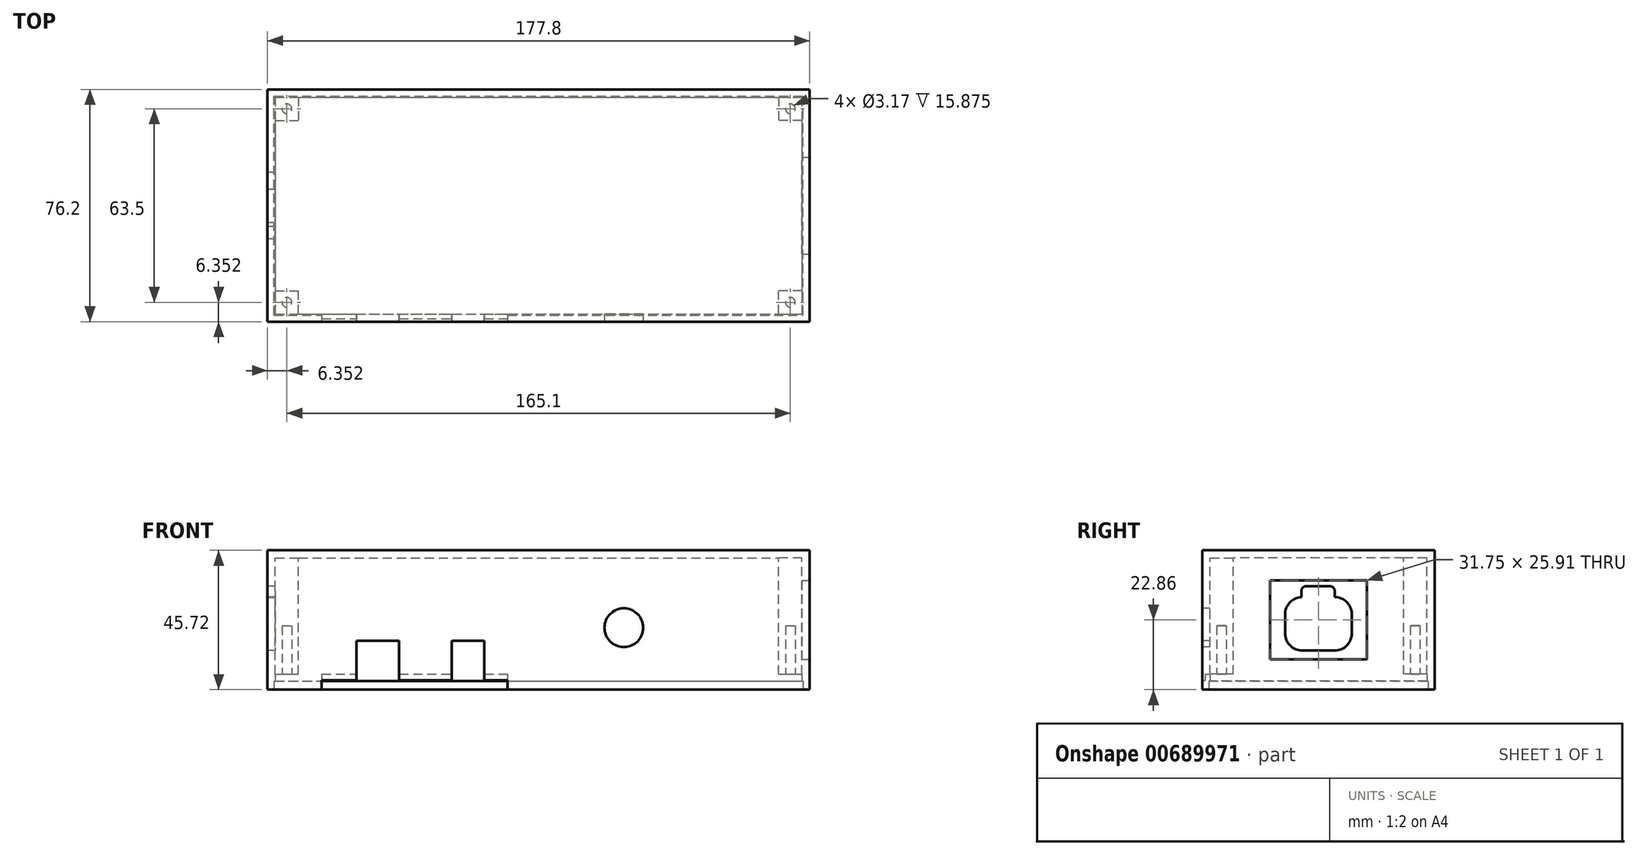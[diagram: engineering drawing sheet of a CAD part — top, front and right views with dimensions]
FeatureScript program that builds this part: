
annotation { "Feature Type Name" : "Feature", "Feature Type Description" : "" }
export const myFeature = defineFeature(function(context is Context, id is Id, definition is map)
    precondition{}
    {
        {
            var Q0;
            Q0=qCreatedBy(makeId("Top.planeOp"),FACE);
            var sketch = newSketch(context, id + "F0", { "sketchPlane" : qUnion([Q0])});
            skLineSegment(sketch, "E0.bottom", {"start": v(-143.67, 49.46) * mm, "end": v(34.13, 49.46) * mm});
            skLineSegment(sketch, "E0.top", {"start": v(-143.67, -26.74) * mm, "end": v(34.13, -26.74) * mm});
            skLineSegment(sketch, "E0.left", {"start": v(-143.67, 49.46) * mm, "end": v(-143.67, -26.74) * mm});
            skLineSegment(sketch, "E0.right", {"start": v(34.13, 49.46) * mm, "end": v(34.13, -26.74) * mm});
            skSolve(sketch);
        }
        {
            var Q0;
            Q0=makeQuery(id+"F0.imprint","IMPRINT",FACE,{"disambiguationData":[TD([[makeQuery(id+"F0.imprint","IMPRINT",EDGE,{"derivedFrom":sQuery(id+"F0.wireOp",EDGE,"E0.bottom")}),-1.0]])]});
            extrude(context, id + "F1", {"entities" : qUnion([Q0]), "depth" : 45.72 * mm, "offsetDistance" : 25.4 * mm});
        }
        {
            var Q0;
            Q0=makeQuery(id+"F1.opExtrude","CAP_FACE",FACE,{"disambiguationData":[OSD([sQuery(id+"F0.wireOp",EDGE,"E0.bottom"),sQuery(id+"F0.wireOp",EDGE,"E0.top"),sQuery(id+"F0.wireOp",EDGE,"E0.left"),sQuery(id+"F0.wireOp",EDGE,"E0.right")])],"isStart":true});
            shell(context, id + "F2", {"entities" : qUnion([Q0]), "thickness" : 2.54 * mm});
        }
        {
            var Q0;
            Q0=makeQuery(id+"F1.opExtrude","SWEPT_FACE",FACE,{"disambiguationData":[OSD([sQuery(id+"F0.wireOp",EDGE,"E0.top")])]});
            var sketch = newSketch(context, id + "F3", { "sketchPlane" : qUnion([Q0])});
            skLineSegment(sketch, "E1.bottom", {"start": v(-114.46, 0) * mm, "end": v(-100.49, 0) * mm});
            skLineSegment(sketch, "E1.top", {"start": v(-114.46, 16) * mm, "end": v(-100.49, 16) * mm});
            skLineSegment(sketch, "E1.left", {"start": v(-114.46, 0) * mm, "end": v(-114.46, 16) * mm});
            skLineSegment(sketch, "E1.right", {"start": v(-100.49, 0) * mm, "end": v(-100.49, 16) * mm});
            skLineSegment(sketch, "E2.bottom", {"start": v(-83.22, 0) * mm, "end": v(-72.55, 0) * mm});
            skLineSegment(sketch, "E2.top", {"start": v(-83.22, 16) * mm, "end": v(-72.55, 16) * mm});
            skLineSegment(sketch, "E2.left", {"start": v(-83.22, 0) * mm, "end": v(-83.22, 16) * mm});
            skLineSegment(sketch, "E2.right", {"start": v(-72.55, 0) * mm, "end": v(-72.55, 16) * mm});
            skSolve(sketch);
        }
        {
            var Q0;
            Q0=makeQuery(id+"F3.imprint","IMPRINT",FACE,{"disambiguationData":[TD([[makeQuery(id+"F3.imprint","IMPRINT",EDGE,{"derivedFrom":sQuery(id+"F3.wireOp",EDGE,"E1.bottom")}),1.0]])]});
            var Q1;
            Q1=makeQuery(id+"F3.imprint","IMPRINT",FACE,{"disambiguationData":[TD([[makeQuery(id+"F3.imprint","IMPRINT",EDGE,{"derivedFrom":sQuery(id+"F3.wireOp",EDGE,"E2.bottom")}),1.0]])]});
            extrude(context, id + "F4", {"entities" : qUnion([Q0, Q1]), "operationType" : NewBodyOperationType.REMOVE, "oppositeDirection" : true, "depth" : 2.54 * mm, "offsetDistance" : 25.4 * mm});
        }
        {
            var Q0;
            {var subQ0=sQuery(id+"F0.wireOp",EDGE,"E0.left");var subQ1=sQuery(id+"F0.wireOp",EDGE,"E0.bottom");var subQ2=sQuery(id+"F0.wireOp",EDGE,"E0.top");var subQ3=sQuery(id+"F0.wireOp",EDGE,"E0.right");Q0=makeQuery(id+"F4.boolean.opBoolean","SPLIT",FACE,{"disambiguationData":[TD([makeQuery(id+"F1.opExtrude","SWEPT_FACE",FACE,{"disambiguationData":[OSD([subQ1])]})])],"derivedFrom":makeQuery(id+"F1.opExtrude","CAP_FACE",FACE,{"disambiguationData":[OSD([subQ1,subQ2,subQ0,subQ3])],"isStart":true})});}
            var sketch = newSketch(context, id + "F5", { "sketchPlane" : qUnion([Q0])});
            skLineSegment(sketch, "E3.bottom", {"start": v(-125.89, 24.2) * mm, "end": v(-64.93, 24.2) * mm});
            skLineSegment(sketch, "E3.top", {"start": v(-125.89, 26.74) * mm, "end": v(-64.93, 26.74) * mm});
            skLineSegment(sketch, "E3.left", {"start": v(-125.89, 24.2) * mm, "end": v(-125.89, 26.74) * mm});
            skLineSegment(sketch, "E3.right", {"start": v(-64.93, 24.2) * mm, "end": v(-64.93, 26.74) * mm});
            skSolve(sketch);
        }
        {
            var Q0;
            {var subQ5=sQuery(id+"F5.wireOp",EDGE,"E3.left");Q0=makeQuery(id+"F5.imprint","IMPRINT",FACE,{"disambiguationData":[TD([[makeQuery(id+"F5.imprint","IMPRINT",EDGE,{"derivedFrom":subQ5}),-1.0]])]});}
            var Q1;
            {var subQ0=sQuery(id+"F5.wireOp",EDGE,"E3.bottom");var subQ1=sQuery(id+"F0.wireOp",EDGE,"E0.top");var subQ2=makeQuery(id+"F4.boolean.opBoolean","COPY",EDGE,{"derivedFrom":makeQuery(id+"F4.opExtrude","SWEPT_EDGE",EDGE,{"disambiguationData":[OSD([subQ1,sQuery(id+"F3.wireOp",EDGE,"E1.bottom"),sQuery(id+"F3.wireOp",EDGE,"E1.left")])]})});var subQ3=makeQuery(id+"F5.imprint","INTERSECT",VERTEX,{"derivedFrom":[subQ2,subQ0]});Q1=makeQuery(id+"F5.imprint","IMPRINT",FACE,{"disambiguationData":[TD([[makeQuery(id+"F5.imprint","IMPRINT",EDGE,{"disambiguationData":[TD([[subQ3,-1.0]])],"derivedFrom":subQ0}),1.0]])]});}
            var Q2;
            {var subQ5=sQuery(id+"F5.wireOp",EDGE,"E3.right");Q2=makeQuery(id+"F5.imprint","IMPRINT",FACE,{"disambiguationData":[TD([[makeQuery(id+"F5.imprint","IMPRINT",EDGE,{"derivedFrom":subQ5}),1.0]])]});}
            extrude(context, id + "F6", {"entities" : qUnion([Q0, Q1, Q2]), "operationType" : NewBodyOperationType.REMOVE, "oppositeDirection" : true, "depth" : 3.05 * mm, "offsetDistance" : 25.4 * mm});
        }
        {
            var Q0;
            Q0=makeQuery(id+"F1.opExtrude","SWEPT_FACE",FACE,{"disambiguationData":[OSD([sQuery(id+"F0.wireOp",EDGE,"E0.left")])]});
            var sketch = newSketch(context, id + "F7", { "sketchPlane" : qUnion([Q0])});
            skLineSegment(sketch, "E4.bottom", {"start": v(-16.7, 30.35) * mm, "end": v(-6.04, 30.35) * mm});
            skLineSegment(sketch, "E4.top", {"start": v(-16.7, 12.83) * mm, "end": v(-6.03, 12.83) * mm});
            skLineSegment(sketch, "E4.left", {"start": v(-22.28, 24.77) * mm, "end": v(-22.28, 18.41) * mm});
            skLineSegment(sketch, "E4.right", {"start": v(-0.44, 24.77) * mm, "end": v(-0.44, 18.41) * mm});
            skPoint(sketch, "E5.visualSharp", {"position": v(-22.28, 30.35) * mm});
            skArc(sketch, "E5.filletArc", {"start": v(-16.7, 30.35) * mm, "mid": v(-20.65, 28.72) * mm, "end": v(-22.28, 24.77) * mm});
            skPoint(sketch, "E6.visualSharp", {"position": v(-0.44, 30.35) * mm});
            skArc(sketch, "E6.filletArc", {"start": v(-0.44, 24.77) * mm, "mid": v(-1.56, 28.12) * mm, "end": v(-4.46, 30.13) * mm});
            skPoint(sketch, "E7.visualSharp", {"position": v(-0.44, 12.83) * mm});
            skArc(sketch, "E7.filletArc", {"start": v(-6.03, 12.83) * mm, "mid": v(-2.08, 14.46) * mm, "end": v(-0.44, 18.41) * mm});
            skPoint(sketch, "E8.visualSharp", {"position": v(-22.28, 12.83) * mm});
            skArc(sketch, "E8.filletArc", {"start": v(-22.28, 18.41) * mm, "mid": v(-20.65, 14.46) * mm, "end": v(-16.7, 12.83) * mm});
            skLineSegment(sketch, "E9.bottom", {"start": v(-15.17, 33.9) * mm, "end": v(-7.3, 33.9) * mm});
            skLineSegment(sketch, "E9.top", {"start": v(-16.7, 30.35) * mm, "end": v(-5.77, 30.35) * mm});
            skLineSegment(sketch, "E9.left", {"start": v(-16.7, 32.39) * mm, "end": v(-16.7, 30.35) * mm});
            skLineSegment(sketch, "E9.right", {"start": v(-5.77, 32.39) * mm, "end": v(-5.77, 30.35) * mm});
            skPoint(sketch, "E10.visualSharp", {"position": v(-16.7, 33.9) * mm});
            skArc(sketch, "E10.filletArc", {"start": v(-15.17, 33.9) * mm, "mid": v(-16.25, 33.46) * mm, "end": v(-16.7, 32.39) * mm});
            skPoint(sketch, "E11.visualSharp", {"position": v(-5.77, 33.9) * mm});
            skArc(sketch, "E11.filletArc", {"start": v(-5.77, 32.39) * mm, "mid": v(-6.22, 33.46) * mm, "end": v(-7.3, 33.9) * mm});
            skLineSegment(sketch, "E12", {"start": v(-5.77, 30.35) * mm, "end": v(-4.46, 30.13) * mm});
            skLineSegment(sketch, "E13", {"start": v(26.74, 22.86) * mm, "end": v(-0.44, 22.86) * mm, "construction": true});
            skPoint(sketch, "E13.endSnap0", {"position": v(-0.44, 21.59) * mm});
            skLineSegment(sketch, "E14", {"start": v(-11.36, 0) * mm, "end": v(-11.36, 12.83) * mm, "construction": true});
            skLineSegment(sketch, "E15", {"start": v(-16.7, 24.77) * mm, "end": v(-6.03, 18.41) * mm, "construction": true});
            skLineSegment(sketch, "E16", {"start": v(-6.03, 24.77) * mm, "end": v(-16.7, 18.41) * mm, "construction": true});
            skLineSegment(sketch, "E17.bottom", {"start": v(-0.44, 30.35) * mm, "end": v(-22.28, 30.35) * mm});
            skLineSegment(sketch, "E17.top", {"start": v(-0.44, 12.83) * mm, "end": v(-22.28, 12.83) * mm});
            skLineSegment(sketch, "E17.left", {"start": v(-0.44, 30.35) * mm, "end": v(-0.44, 12.83) * mm});
            skLineSegment(sketch, "E17.right", {"start": v(-22.28, 30.35) * mm, "end": v(-22.28, 12.83) * mm});
            skPoint(sketch, "E18", {"position": v(-11.36, 21.6) * mm});
            skSolve(sketch);
        }
        {
            var Q0;
            Q0=makeQuery(id+"F7.imprint","IMPRINT",FACE,{"disambiguationData":[TD([[makeQuery(id+"F7.imprint","IMPRINT",EDGE,{"derivedFrom":sQuery(id+"F7.wireOp",EDGE,"E9.bottom")}),-1.0]])]});
            var Q1;
            {var subQ4=sQuery(id+"F7.wireOp",EDGE,"E5.filletArc");Q1=makeQuery(id+"F7.imprint","IMPRINT",FACE,{"disambiguationData":[TD([[makeQuery(id+"F7.imprint","IMPRINT",EDGE,{"derivedFrom":subQ4}),1.0]])]});}
            extrude(context, id + "F8", {"entities" : qUnion([Q0, Q1]), "operationType" : NewBodyOperationType.REMOVE, "oppositeDirection" : true, "depth" : 2.54 * mm, "offsetDistance" : 25.4 * mm});
        }
        {
            var Q0;
            Q0=makeQuery(id+"F1.opExtrude","SWEPT_FACE",FACE,{"disambiguationData":[OSD([sQuery(id+"F0.wireOp",EDGE,"E0.right")])]});
            var sketch = newSketch(context, id + "F9", { "sketchPlane" : qUnion([Q0])});
            skLineSegment(sketch, "E19.bottom", {"start": v(-4.51, 35.81) * mm, "end": v(27.24, 35.81) * mm});
            skLineSegment(sketch, "E19.top", {"start": v(-4.51, 9.9) * mm, "end": v(27.24, 9.9) * mm});
            skLineSegment(sketch, "E19.left", {"start": v(-4.51, 35.81) * mm, "end": v(-4.51, 9.9) * mm});
            skLineSegment(sketch, "E19.right", {"start": v(27.24, 35.81) * mm, "end": v(27.24, 9.9) * mm});
            skLineSegment(sketch, "E20", {"start": v(27.24, 22.86) * mm, "end": v(49.46, 22.86) * mm, "construction": true});
            skLineSegment(sketch, "E21", {"start": v(11.36, 9.9) * mm, "end": v(11.36, 0) * mm, "construction": true});
            skSolve(sketch);
        }
        {
            var Q0;
            Q0=makeQuery(id+"F9.imprint","IMPRINT",FACE,{"disambiguationData":[TD([[makeQuery(id+"F9.imprint","IMPRINT",EDGE,{"derivedFrom":sQuery(id+"F9.wireOp",EDGE,"E19.bottom")}),-1.0]])]});
            extrude(context, id + "F10", {"entities" : qUnion([Q0]), "operationType" : NewBodyOperationType.REMOVE, "oppositeDirection" : true, "depth" : 2.54 * mm, "offsetDistance" : 25.4 * mm});
        }
        {
            var Q0;
            {var subQ0=sQuery(id+"F0.wireOp",EDGE,"E0.left");var subQ1=sQuery(id+"F0.wireOp",EDGE,"E0.bottom");var subQ2=sQuery(id+"F0.wireOp",EDGE,"E0.top");var subQ3=sQuery(id+"F0.wireOp",EDGE,"E0.right");Q0=makeQuery(id+"F4.boolean.opBoolean","SPLIT",FACE,{"disambiguationData":[TD([makeQuery(id+"F1.opExtrude","SWEPT_FACE",FACE,{"disambiguationData":[OSD([subQ1])]})])],"derivedFrom":makeQuery(id+"F1.opExtrude","CAP_FACE",FACE,{"disambiguationData":[OSD([subQ1,subQ2,subQ0,subQ3])],"isStart":true})});}
            var sketch = newSketch(context, id + "F11", { "sketchPlane" : qUnion([Q0])});
            skPoint(sketch, "E22.firstSnap0", {"position": v(-125.89, 25.75) * mm});
            skLineSegment(sketch, "E22.bottom", {"start": v(-125.89, 25.75) * mm, "end": v(-62.39, 25.75) * mm});
            skLineSegment(sketch, "E22.top", {"start": v(-125.89, 24.2) * mm, "end": v(-62.39, 24.2) * mm});
            skLineSegment(sketch, "E22.left", {"start": v(-125.89, 25.75) * mm, "end": v(-125.89, 24.2) * mm});
            skLineSegment(sketch, "E22.right", {"start": v(-62.39, 25.75) * mm, "end": v(-62.39, 24.2) * mm});
            skSolve(sketch);
        }
        {
            var Q0;
            {var subQ0=sQuery(id+"F11.wireOp",EDGE,"E22.left");Q0=makeQuery(id+"F11.imprint","IMPRINT",FACE,{"disambiguationData":[TD([[makeQuery(id+"F11.imprint","IMPRINT",EDGE,{"derivedFrom":subQ0}),-1.0]])]});}
            extrude(context, id + "F12", {"entities" : qUnion([Q0]), "operationType" : NewBodyOperationType.REMOVE, "oppositeDirection" : true, "depth" : 5.08 * mm, "offsetDistance" : 25.4 * mm});
        }
        {
            var Q0;
            Q0=makeQuery(id+"F2.opShell","OFFSET_FACE",FACE,{"disambiguationData":[OSD([sQuery(id+"F0.wireOp",EDGE,"E0.bottom"),sQuery(id+"F0.wireOp",EDGE,"E0.top"),sQuery(id+"F0.wireOp",EDGE,"E0.left"),sQuery(id+"F0.wireOp",EDGE,"E0.right")])]});
            var sketch = newSketch(context, id + "F13", { "sketchPlane" : qUnion([Q0])});
            skLineSegment(sketch, "E23.bottom", {"start": v(-141.13, 24.2) * mm, "end": v(-133.5, 24.2) * mm});
            skLineSegment(sketch, "E23.top", {"start": v(-141.13, 16.58) * mm, "end": v(-133.5, 16.58) * mm});
            skLineSegment(sketch, "E23.left", {"start": v(-141.13, 24.2) * mm, "end": v(-141.13, 16.58) * mm});
            skLineSegment(sketch, "E23.right", {"start": v(-133.5, 24.2) * mm, "end": v(-133.5, 16.58) * mm});
            skLineSegment(sketch, "E24.bottom", {"start": v(31.6, 24.2) * mm, "end": v(23.97, 24.2) * mm});
            skLineSegment(sketch, "E24.top", {"start": v(31.6, 16.58) * mm, "end": v(23.97, 16.58) * mm});
            skLineSegment(sketch, "E24.left", {"start": v(31.6, 24.2) * mm, "end": v(31.6, 16.58) * mm});
            skLineSegment(sketch, "E24.right", {"start": v(23.97, 24.2) * mm, "end": v(23.97, 16.58) * mm});
            skLineSegment(sketch, "E25.bottom", {"start": v(31.6, -46.92) * mm, "end": v(23.97, -46.92) * mm});
            skLineSegment(sketch, "E25.top", {"start": v(31.6, -39.3) * mm, "end": v(23.97, -39.3) * mm});
            skLineSegment(sketch, "E25.left", {"start": v(31.6, -46.92) * mm, "end": v(31.6, -39.3) * mm});
            skLineSegment(sketch, "E25.right", {"start": v(23.97, -46.92) * mm, "end": v(23.97, -39.3) * mm});
            skLineSegment(sketch, "E26.bottom", {"start": v(-141.13, -46.92) * mm, "end": v(-133.5, -46.92) * mm});
            skLineSegment(sketch, "E26.top", {"start": v(-141.13, -39.3) * mm, "end": v(-133.5, -39.3) * mm});
            skLineSegment(sketch, "E26.left", {"start": v(-141.13, -46.92) * mm, "end": v(-141.13, -39.3) * mm});
            skLineSegment(sketch, "E26.right", {"start": v(-133.5, -46.92) * mm, "end": v(-133.5, -39.3) * mm});
            skSolve(sketch);
        }
        {
            var Q0;
            Q0=makeQuery(id+"F13.imprint","IMPRINT",FACE,{"disambiguationData":[TD([[makeQuery(id+"F13.imprint","IMPRINT",EDGE,{"derivedFrom":sQuery(id+"F13.wireOp",EDGE,"E24.bottom")}),-1.0]])]});
            var Q1;
            Q1=makeQuery(id+"F13.imprint","IMPRINT",FACE,{"disambiguationData":[TD([[makeQuery(id+"F13.imprint","IMPRINT",EDGE,{"derivedFrom":sQuery(id+"F13.wireOp",EDGE,"E25.bottom")}),1.0]])]});
            var Q2;
            Q2=makeQuery(id+"F13.imprint","IMPRINT",FACE,{"disambiguationData":[TD([[makeQuery(id+"F13.imprint","IMPRINT",EDGE,{"derivedFrom":sQuery(id+"F13.wireOp",EDGE,"E23.bottom")}),-1.0]])]});
            var Q3;
            Q3=makeQuery(id+"F13.imprint","IMPRINT",FACE,{"disambiguationData":[TD([[makeQuery(id+"F13.imprint","IMPRINT",EDGE,{"derivedFrom":sQuery(id+"F13.wireOp",EDGE,"E26.bottom")}),1.0]])]});
            extrude(context, id + "F14", {"entities" : qUnion([Q0, Q1, Q2, Q3]), "operationType" : NewBodyOperationType.ADD, "depth" : 38.1 * mm, "offsetDistance" : 25.4 * mm});
        }
        {
            var Q0;
            Q0=makeQuery(id+"F14.opExtrude","CAP_FACE",FACE,{"disambiguationData":[OSD([sQuery(id+"F13.wireOp",EDGE,"E23.bottom"),sQuery(id+"F13.wireOp",EDGE,"E23.top"),sQuery(id+"F13.wireOp",EDGE,"E23.left"),sQuery(id+"F13.wireOp",EDGE,"E23.right")])],"isStart":false});
            var sketch = newSketch(context, id + "F15", { "sketchPlane" : qUnion([Q0])});
            skCircle(sketch, "E27", {"center": v(-137.32, 20.39) * mm, "radius": 1.59 * mm});
            skPoint(sketch, "E27.centerSnap0", {"position": v(-137.32, 24.2) * mm});
            skPoint(sketch, "E27.centerSnap1", {"position": v(-133.5, 20.39) * mm});
            skCircle(sketch, "E28", {"center": v(27.78, 20.39) * mm, "radius": 1.59 * mm});
            skCircle(sketch, "E29", {"center": v(-137.32, -43.11) * mm, "radius": 1.59 * mm});
            skCircle(sketch, "E30", {"center": v(27.78, -43.11) * mm, "radius": 1.59 * mm});
            skSolve(sketch);
        }
        {
            var Q0;
            Q0=makeQuery(id+"F15.imprint","IMPRINT",FACE,{"disambiguationData":[TD([[makeQuery(id+"F15.imprint","IMPRINT",EDGE,{"derivedFrom":sQuery(id+"F15.wireOp",EDGE,"E27")}),1.0]])]});
            var Q1;
            Q1=makeQuery(id+"F15.imprint","IMPRINT",FACE,{"disambiguationData":[TD([[makeQuery(id+"F15.imprint","IMPRINT",EDGE,{"derivedFrom":sQuery(id+"F15.wireOp",EDGE,"E29")}),1.0]])]});
            var Q2;
            Q2=makeQuery(id+"F15.imprint","IMPRINT",FACE,{"disambiguationData":[TD([[makeQuery(id+"F15.imprint","IMPRINT",EDGE,{"derivedFrom":sQuery(id+"F15.wireOp",EDGE,"E28")}),1.0]])]});
            var Q3;
            Q3=makeQuery(id+"F15.imprint","IMPRINT",FACE,{"disambiguationData":[TD([[makeQuery(id+"F15.imprint","IMPRINT",EDGE,{"derivedFrom":sQuery(id+"F15.wireOp",EDGE,"E30")}),1.0]])]});
            extrude(context, id + "F16", {"entities" : qUnion([Q0, Q1, Q2, Q3]), "operationType" : NewBodyOperationType.REMOVE, "oppositeDirection" : true, "depth" : 15.88 * mm, "offsetDistance" : 25.4 * mm});
        }
        {
            var Q0;
            Q0=makeQuery(id+"F1.opExtrude","SWEPT_FACE",FACE,{"disambiguationData":[OSD([sQuery(id+"F0.wireOp",EDGE,"E0.top")])]});
            var sketch = newSketch(context, id + "F17", { "sketchPlane" : qUnion([Q0])});
            skCircle(sketch, "E31", {"center": v(-26.83, 20.32) * mm, "radius": 6.35 * mm});
            skSolve(sketch);
        }
        {
            var Q0;
            Q0=makeQuery(id+"F17.imprint","IMPRINT",FACE,{"disambiguationData":[TD([[makeQuery(id+"F17.imprint","IMPRINT",EDGE,{"derivedFrom":sQuery(id+"F17.wireOp",EDGE,"E31")}),1.0]])]});
            extrude(context, id + "F18", {"entities" : qUnion([Q0]), "operationType" : NewBodyOperationType.REMOVE, "oppositeDirection" : true, "depth" : 2.54 * mm, "offsetDistance" : 25.4 * mm});
        }
        {
            var Q0;
            {var subQ0=sQuery(id+"F0.wireOp",EDGE,"E0.left");var subQ1=sQuery(id+"F0.wireOp",EDGE,"E0.bottom");var subQ2=sQuery(id+"F0.wireOp",EDGE,"E0.top");var subQ3=sQuery(id+"F0.wireOp",EDGE,"E0.right");Q0=makeQuery(id+"F4.boolean.opBoolean","SPLIT",FACE,{"disambiguationData":[TD([makeQuery(id+"F1.opExtrude","SWEPT_FACE",FACE,{"disambiguationData":[OSD([subQ1])]})])],"derivedFrom":makeQuery(id+"F1.opExtrude","CAP_FACE",FACE,{"disambiguationData":[OSD([subQ1,subQ2,subQ0,subQ3])],"isStart":true})});}
            var sketch = newSketch(context, id + "F19", { "sketchPlane" : qUnion([Q0])});
            skLineSegment(sketch, "E32.bottom", {"start": v(-141.5, 24.58) * mm, "end": v(31.97, 24.58) * mm});
            skLineSegment(sketch, "E32.top", {"start": v(-141.5, -47.3) * mm, "end": v(31.97, -47.3) * mm});
            skLineSegment(sketch, "E32.left", {"start": v(-141.5, 24.58) * mm, "end": v(-141.5, -47.3) * mm});
            skLineSegment(sketch, "E32.right", {"start": v(31.97, 24.58) * mm, "end": v(31.97, -47.3) * mm});
            skSolve(sketch);
        }
        {
            var Q0;
            Q0=makeQuery(id+"F19.imprint","IMPRINT",FACE,{"disambiguationData":[TD([[makeQuery(id+"F19.imprint","IMPRINT",EDGE,{"derivedFrom":sQuery(id+"F19.wireOp",EDGE,"E32.top")}),1.0]])]});
            extrude(context, id + "F20", {"entities" : qUnion([Q0]), "operationType" : NewBodyOperationType.REMOVE, "oppositeDirection" : true, "depth" : 2.8 * mm, "offsetDistance" : 25.4 * mm});
        }
    });
